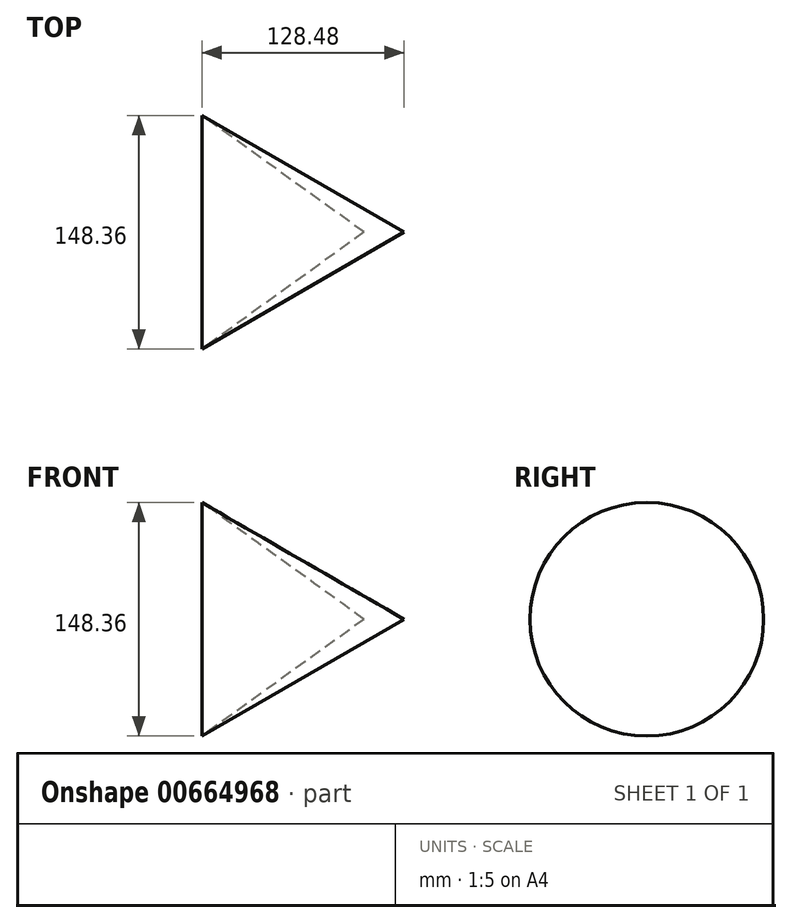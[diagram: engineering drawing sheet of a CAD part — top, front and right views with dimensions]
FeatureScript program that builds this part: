
annotation { "Feature Type Name" : "Feature", "Feature Type Description" : "" }
export const myFeature = defineFeature(function(context is Context, id is Id, definition is map)
    precondition{}
    {
        {
            var Q0;
            Q0=qCreatedBy(makeId("Front.planeOp"),FACE);
            var sketch = newSketch(context, id + "F0", { "sketchPlane" : qUnion([Q0])});
            skLineSegment(sketch, "E0", {"start": v(0, 0) * mm, "end": v(25.4, 0) * mm});
            skLineSegment(sketch, "E1", {"start": v(25.4, 0) * mm, "end": v(-103.08, 74.18) * mm});
            skLineSegment(sketch, "E2", {"start": v(-103.08, 74.18) * mm, "end": v(0, 0) * mm});
            skSolve(sketch);
        }
        {
            var Q0;
            Q0 = qSketchRegion(id + "F0", true);
            var Q1;
            Q1=sQuery(id+"F0.wireOp",EDGE,"E0");
            revolve(context, id + "F1", {"surfaceOperationType" : NewSurfaceOperationType.NEW, "entities" : qUnion([Q0]), "axis" : qUnion([Q1]), "revolveType" : RevolveType.FULL});
        }
    });
